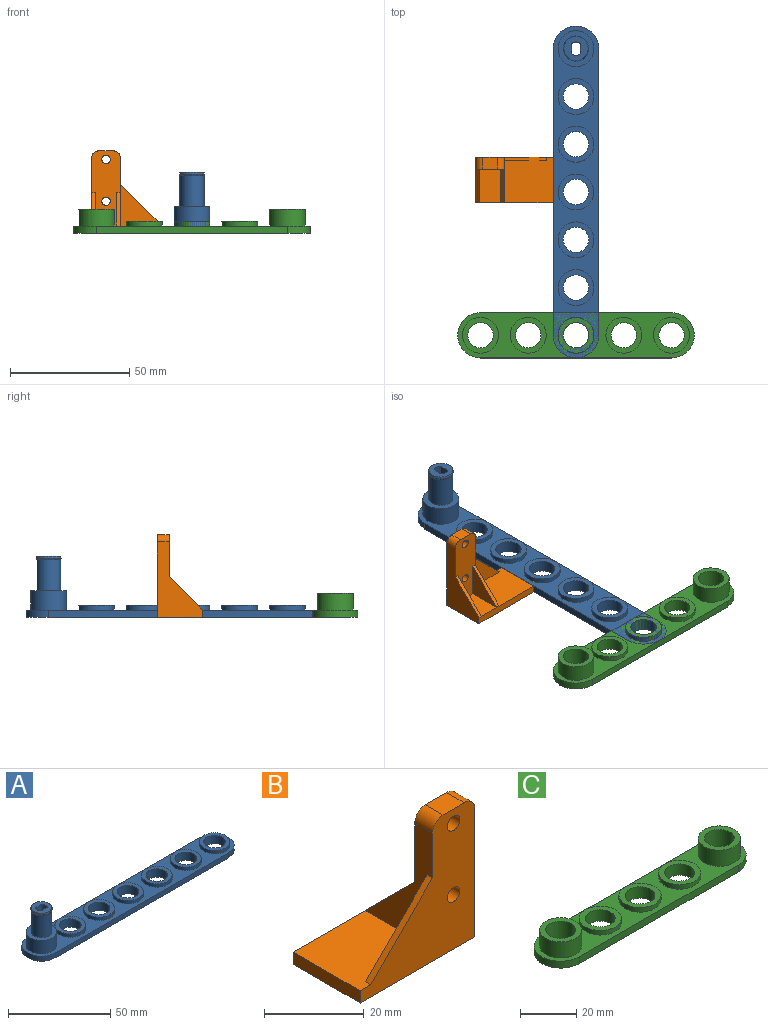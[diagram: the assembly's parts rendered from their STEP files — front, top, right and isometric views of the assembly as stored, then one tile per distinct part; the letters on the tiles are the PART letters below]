
ASSEMBLY  parts=3 mates=1
PART A: 34 faces, bbox 139x19x25.5 mm
  f0: cylinder r=9.5mm len=19mm, axis (0,0,-1), area 89.5mm2, adj f1,f5,f7,f8
  f1: plane 120x3mm, normal (0,1,0), area 360mm2, adj f0,f2,f7,f8
  f2: cylinder r=9.5mm len=19mm, axis (0,0,-1), area 89.5mm2, adj f1,f5,f7,f8
  f3: cylinder r=5.3mm len=10.6mm, axis (0,0,-1), area 166.5mm2, adj f8,f13
  f4: cylinder r=5.3mm len=10.6mm, axis (0,0,-1), area 166.5mm2, adj f8,f11
  f5: plane 120x3mm, normal (0,-1,0), area 360mm2, adj f0,f2,f7,f8
  f6: cylinder r=5.3mm len=10.6mm, axis (0,0,-1), area 166.5mm2, adj f8,f15
  f7: plane 139x19mm, normal (0,0,1), area 1326.5mm2, adj f0,f1,f2,f5,f9,f10,f12,f14
  f8: plane 139x19mm, normal (0,0,-1), area 2014.5mm2, adj f0,f1,f2,f3,f4,f5,f6,f16
  f9: cylinder r=7.5mm len=15mm, axis (0,0,-1), area 377mm2, adj f7,f30
  f10: cylinder r=7.5mm len=15mm, axis (0,0,-1), area 94.2mm2, adj f7,f11
  f11: plane 15x15mm, normal (0,0,1), area 88.5mm2, adj f4,f10
  f12: cylinder r=7.5mm len=15mm, axis (0,0,-1), area 94.2mm2, adj f7,f13
  f13: plane 15x15mm, normal (0,0,1), area 88.5mm2, adj f3,f12
  f14: cylinder r=7.5mm len=15mm, axis (0,0,-1), area 94.2mm2, adj f7,f15
  f15: plane 15x15mm, normal (0,0,1), area 88.5mm2, adj f6,f14
  f16: cylinder r=5.3mm len=10.6mm, axis (0,0,-1), area 166.5mm2, adj f8,f18
  f17: cylinder r=7.5mm len=15mm, axis (0,0,-1), area 94.2mm2, adj f7,f18
  f18: plane 15x15mm, normal (0,0,1), area 88.5mm2, adj f16,f17
  f19: cylinder r=5.3mm len=10.6mm, axis (0,0,-1), area 166.5mm2, adj f8,f21
  f20: cylinder r=7.5mm len=15mm, axis (0,0,-1), area 94.2mm2, adj f7,f21
  f21: plane 15x15mm, normal (0,0,1), area 88.5mm2, adj f19,f20
  f22: cylinder r=5.3mm len=10.6mm, axis (0,0,-1), area 166.5mm2, adj f8,f24
  f23: cylinder r=7.5mm len=15mm, axis (0,0,-1), area 94.2mm2, adj f7,f24
  f24: plane 15x15mm, normal (0,0,1), area 88.5mm2, adj f22,f23
  f25: cylinder r=5.05mm len=13mm, axis (0,0,-1), area 412.5mm2, adj f30,f32
  f26: cylinder r=2.8mm len=25.5mm, axis (0,0,-1), area 106.5mm2, adj f8,f27,f29,f31
  f27: plane 25.5x4.11mm, normal (0,-1,0), area 104.9mm2, adj f8,f26,f28,f31
  f28: cylinder r=2.8mm len=25.5mm, axis (0,0,-1), area 106.5mm2, adj f8,f27,f29,f31
  f29: plane 25.5x4.11mm, normal (0,1,0), area 104.9mm2, adj f8,f26,f28,f31
  f30: plane 15x15mm, normal (0,0,1), area 96.6mm2, adj f9,f25
  f31: plane 10.1x10.1mm, normal (0,0,1), area 60.6mm2, adj f26,f27,f28,f29,f33
  f32: cone r=5.3mm half-angle=18.4deg, axis (0,0,1), area 25.7mm2, adj f25,f33
  f33: cone r=5.05mm half-angle=18.4deg, axis (0,0,-1), area 25.7mm2, adj f31,f32
PART B: 20 faces, bbox 32.5x19x34.5 mm
  f0: plane 14x9mm, normal (0,0,1), area 126mm2, adj f1,f5,f14,f15
  f1: plane 31.5x12mm, normal (0,1,0), area 312.9mm2, adj f0,f4,f8,f9,f10,f11,f12,f13
  f2: plane 20.5x19mm, normal (0,0,1), area 363.2mm2, adj f3,f5,f6,f8,f16,f17
  f3: plane 34.5x32.5mm, normal (0,-1,0), area 605.5mm2, adj f2,f4,f6,f7,f8,f9,f10,f11
  f4: plane 31.5x19mm, normal (1,0,0), area 297.5mm2, adj f1,f3,f5,f7,f9,f18
  f5: plane 32.5x3mm, normal (0,1,0), area 97.5mm2, adj f0,f2,f4,f6,f7,f18,f19
  f6: plane 19x3mm, normal (-1,0,0), area 57mm2, adj f2,f3,f5,f7
  f7: plane 32.5x19mm, normal (0,0,-1), area 617.5mm2, adj f3,f4,f5,f6
  f8: plane 28.5x19mm, normal (-1,0,0), area 214.2mm2, adj f1,f2,f3,f13,f16,f17,f19
  f9: cylinder r=3mm len=5mm, axis (0,-1,0), area 23.6mm2, adj f1,f3,f4,f10
  f10: plane 6x5mm, normal (0,0,1), area 30mm2, adj f1,f3,f9,f13
  f11: cylinder r=1.75mm len=5mm, axis (0,-1,0), area 55mm2, adj f1,f3
  f12: cylinder r=1.75mm len=5mm, axis (0,-1,0), area 55mm2, adj f1,f3
  f13: cylinder r=3mm len=5mm, axis (0,-1,0), area 23.6mm2, adj f1,f3,f8,f10
  f14: plane 14x14mm, normal (-1,0,0), area 98mm2, adj f0,f1,f18
  f15: plane 14x14mm, normal (1,0,0), area 98mm2, adj f0,f1,f19
  f16: plane 17.5x17.5mm, normal (0,1,0), area 153.1mm2, adj f2,f8,f17
  f17: plane 17.5x17.5mm, normal (-0.71,0,0.71), area 37.1mm2, adj f2,f3,f8,f16
  f18: plane 14x14mm, normal (0,0.71,0.71), area 29.7mm2, adj f1,f4,f5,f14
  f19: plane 14x14mm, normal (0,0.71,0.71), area 29.7mm2, adj f1,f5,f8,f15
PART C: 21 faces, bbox 99x19x10 mm
  f0: cylinder r=9.5mm len=19mm, axis (0,0,-1), area 89.5mm2, adj f1,f6,f8,f9
  f1: plane 80x3mm, normal (0,1,0), area 240mm2, adj f0,f2,f8,f9
  f2: cylinder r=9.5mm len=19mm, axis (0,0,-1), area 89.5mm2, adj f1,f6,f8,f9
  f3: cylinder r=5.3mm len=10.6mm, axis (0,0,-1), area 166.5mm2, adj f9,f14
  f4: cylinder r=5.3mm len=10.6mm, axis (0,0,-1), area 166.5mm2, adj f9,f12
  f5: cylinder r=5.3mm len=10.6mm, axis (0,0,-1), area 333mm2, adj f9,f19
  f6: plane 80x3mm, normal (0,-1,0), area 240mm2, adj f0,f2,f8,f9
  f7: cylinder r=5.3mm len=10.6mm, axis (0,0,-1), area 166.5mm2, adj f9,f16
  f8: plane 99x19mm, normal (0,0,1), area 920mm2, adj f0,f1,f2,f6,f10,f11,f13,f15
  f9: plane 99x19mm, normal (0,0,-1), area 1362.3mm2, adj f0,f1,f2,f3,f4,f5,f6,f7
  f10: cylinder r=7.5mm len=15mm, axis (0,0,-1), area 329.9mm2, adj f8,f19
  f11: cylinder r=7.5mm len=15mm, axis (0,0,-1), area 94.2mm2, adj f8,f12
  f12: plane 15x15mm, normal (0,0,1), area 88.5mm2, adj f4,f11
  f13: cylinder r=7.5mm len=15mm, axis (0,0,-1), area 94.2mm2, adj f8,f14
  f14: plane 15x15mm, normal (0,0,1), area 88.5mm2, adj f3,f13
  f15: cylinder r=7.5mm len=15mm, axis (0,0,-1), area 94.2mm2, adj f8,f16
  f16: plane 15x15mm, normal (0,0,1), area 88.5mm2, adj f7,f15
  f17: cylinder r=5.3mm len=10.6mm, axis (0,0,-1), area 333mm2, adj f9,f20
  f18: cylinder r=7.5mm len=15mm, axis (0,0,-1), area 329.9mm2, adj f8,f20
  f19: plane 15x15mm, normal (0,0,1), area 88.5mm2, adj f5,f10
  f20: plane 15x15mm, normal (0,0,1), area 88.5mm2, adj f17,f18
PLACE A rot(axis=(0,0,-1),90deg) t=(0,0,0)mm
PLACE B rot(axis=(0,0,-1),180deg) t=(-22.5,-45.5,0)mm
PLACE C t=(-40,-120,0)mm fixed
MATE fastened B.f6 <-> A.f5  axis (1,0,0) through (-9.5,-55,1.5)mm
